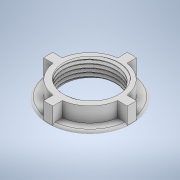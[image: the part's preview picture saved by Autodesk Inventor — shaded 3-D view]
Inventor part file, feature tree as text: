
AUTODESK INVENTOR PART (.ipt)
format: ipt  version: 2020.2 (Build 242310000, 310)  size: 507,904 bytes
history: native  units: mm
features: sketch x4, extrude x2, fillet x1, thread x1, revolve x1, helix x1
ambient origin geometry x8: Origin, YZ Plane, XZ Plane, XY Plane, X Axis, Y Axis, Z Axis, Center Point
bodies: Solid1 (feature_tree), Solid7 (feature_tree)
feature tree (10):
  extrude  "Extrusion1"  Depth=28.034153mm
  extrude  "Extrusion2"  Depth=35.0mm
  fillet  "Fillet1"  Radius=8.0mm
  thread  "Thread7"  [1 undecoded]
  sketch  "Sketch13"  dims[d10=40.0mm d12=360.0deg d23=9.599311mm d43=9.599311mm]
  revolve  "Revolution6"  [1 undecoded]
  helix  "Coil6"  [1 undecoded]
  sketch  "Sketch1"  dims[d0=45.0mm d1=28.034153mm]
  sketch  "Sketch2"  dims[d2=2.0mm d3=0.0mm d4=35.0mm d5=8.0mm d6=0.0mm d9=5.0mm]
  sketch  "Sketch14"  dims[d63=9.599311mm d83=9.599311mm d104=9.599311mm d115=1.0mm d116=10.0mm d117=0.0mm d118=9.599311mm d119=0.320166mm d120=0.320166mm d123=2.0mm d125=9.599311mm d127=0.0mm d128=2.002mm d129=14.0mm d130=10.0mm d131=0.0mm d132=0.0mm d133=0.0mm d134=0.0mm d135=0.0mm]
note: 3 required parameter values undecoded (feature->parameter linkage not recoverable at this tier; creation-order binding heuristic only, values carry confidence <= 0.55)